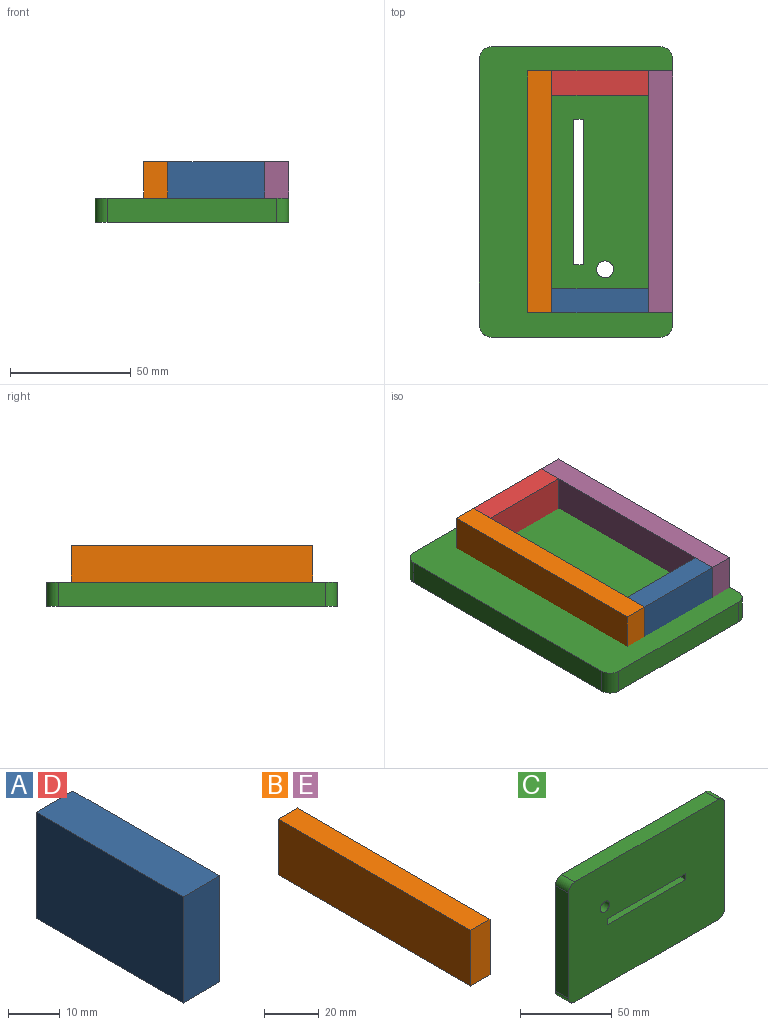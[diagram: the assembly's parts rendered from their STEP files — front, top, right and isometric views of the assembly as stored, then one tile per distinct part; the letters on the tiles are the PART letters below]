
ASSEMBLY  parts=5 mates=4
PART A: 6 faces, bbox 10x40x25 mm
  f0: plane 40x10mm, normal (0,0,1), area 400mm2, adj f1,f3,f4,f5
  f1: plane 40x25mm, normal (-1,0,0), area 1000mm2, adj f0,f2,f4,f5
  f2: plane 40x10mm, normal (0,0,-1), area 400mm2, adj f1,f3,f4,f5
  f3: plane 40x25mm, normal (1,0,0), area 1000mm2, adj f0,f2,f4,f5
  f4: plane 25x10mm, normal (0,-1,0), area 250mm2, adj f0,f1,f2,f3
  f5: plane 25x10mm, normal (0,1,0), area 250mm2, adj f0,f1,f2,f3
PART B: 6 faces, bbox 10x100x25 mm
  f0: plane 100x10mm, normal (0,0,1), area 1000mm2, adj f1,f3,f4,f5
  f1: plane 100x25mm, normal (-1,0,0), area 2500mm2, adj f0,f2,f4,f5
  f2: plane 100x10mm, normal (0,0,-1), area 1000mm2, adj f1,f3,f4,f5
  f3: plane 100x25mm, normal (1,0,0), area 2500mm2, adj f0,f2,f4,f5
  f4: plane 25x10mm, normal (0,-1,0), area 250mm2, adj f0,f1,f2,f3
  f5: plane 25x10mm, normal (0,1,0), area 250mm2, adj f0,f1,f2,f3
PART C: 15 faces, bbox 120x10x80 mm
  f0: plane 120x80mm, normal (0,-1,0), area 9300.1mm2, adj f2,f3,f4,f5,f6,f7,f8,f9
  f1: plane 120x80mm, normal (0,1,0), area 9300.1mm2, adj f2,f3,f4,f5,f6,f7,f8,f9
  f2: plane 110x10mm, normal (0,0,1), area 1100mm2, adj f0,f1,f6,f7
  f3: plane 70x10mm, normal (-1,0,0), area 700mm2, adj f0,f1,f6,f9
  f4: plane 110x10mm, normal (0,0,-1), area 1100mm2, adj f0,f1,f8,f9
  f5: plane 70x10mm, normal (1,0,0), area 700mm2, adj f0,f1,f7,f8
  f6: cylinder r=5mm len=10mm, axis (0,-1,0), area 78.5mm2, adj f0,f1,f2,f3
  f7: cylinder r=5mm len=10mm, axis (0,1,0), area 78.5mm2, adj f0,f1,f2,f5
  f8: cylinder r=5mm len=10mm, axis (0,-1,0), area 78.5mm2, adj f0,f1,f4,f5
  f9: cylinder r=5mm len=10mm, axis (0,1,0), area 78.5mm2, adj f0,f1,f3,f4
  f10: cylinder r=3.5mm len=10mm, axis (0,-1,0), area 219.9mm2, adj f0,f1
  f11: plane 60x10mm, normal (0,0,-1), area 600mm2, adj f0,f1,f12,f14
  f12: plane 10x4mm, normal (1,0,0), area 40mm2, adj f0,f1,f11,f13
  f13: plane 60x10mm, normal (0,0,1), area 600mm2, adj f0,f1,f12,f14
  f14: plane 10x4mm, normal (-1,0,0), area 40mm2, adj f0,f1,f11,f13
PART D: same geometry as A
PART E: same geometry as B
PLACE A rot(axis=(0,0,1),90deg) t=(-144.64,-102.51,18.92)mm
PLACE B t=(-181.43,-26.08,23.96)mm fixed
PLACE C rot(axis=(0.58,0.58,0.58),120deg) t=(-207.09,-1.11,12.98)mm
PLACE D rot(axis=(0.71,0.71,0),180deg) t=(-104.64,-12.51,12.03)mm
PLACE E t=(-131.43,-26.08,23.96)mm
MATE fastened E.f1 <-> A.f4  axis (-1,0,0) through (-104.64,-126.08,15.48)mm
MATE fastened D.f5 <-> E.f1  axis (1,0,0) through (-104.64,-26.08,15.48)mm
MATE fastened A.f5 <-> B.f3  axis (-1,0,0) through (-144.64,-126.08,15.48)mm
MATE fastened E.f2 <-> C.f0  axis (0,0,-1) through (-94.64,-76.08,2.98)mm
